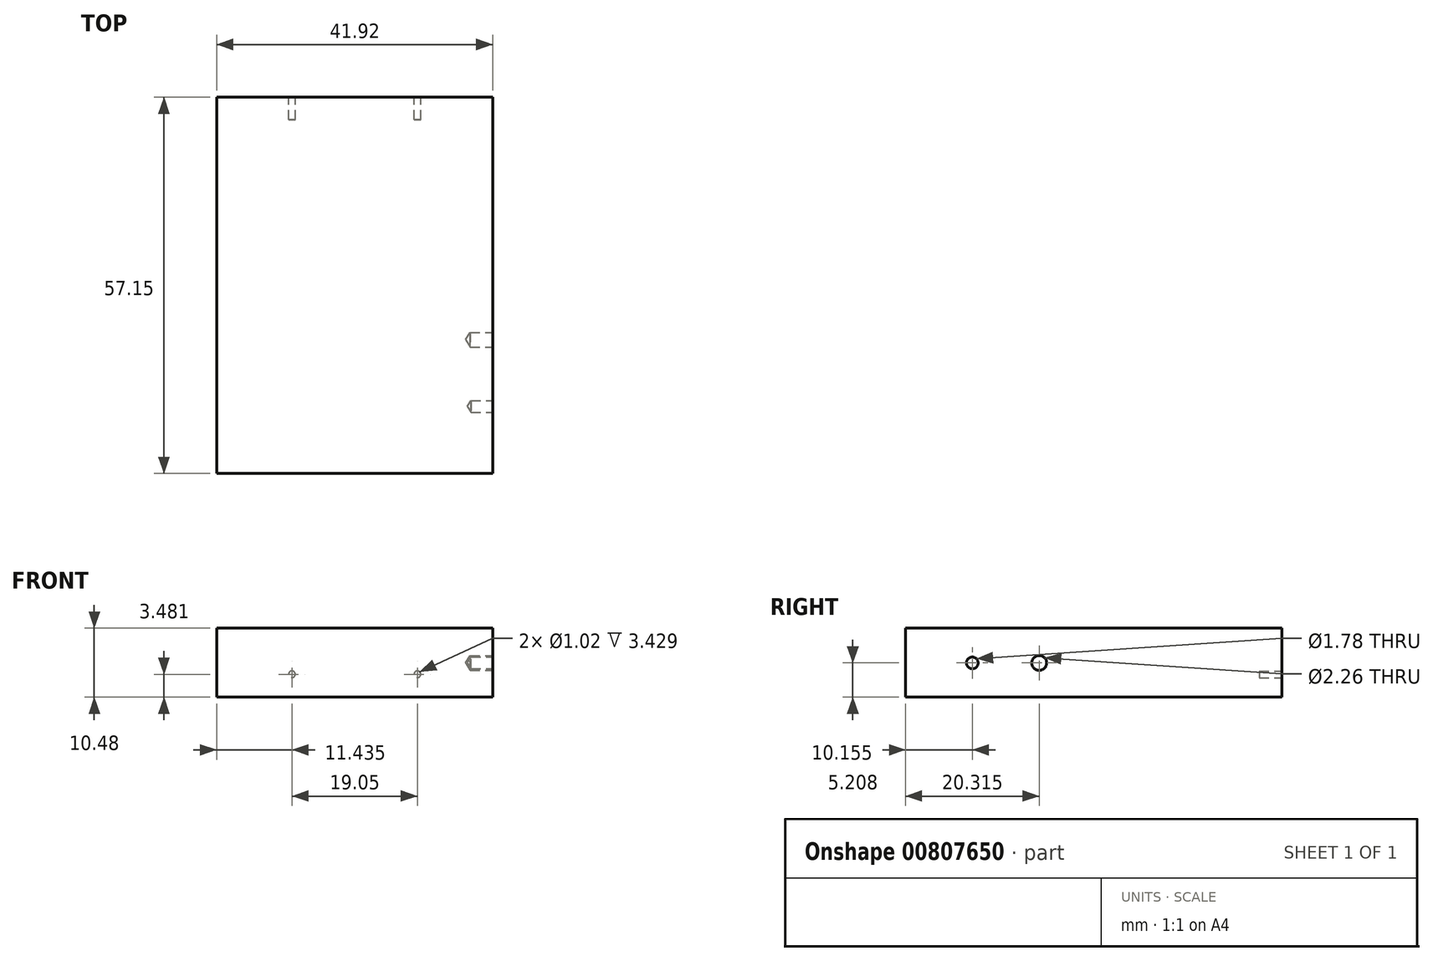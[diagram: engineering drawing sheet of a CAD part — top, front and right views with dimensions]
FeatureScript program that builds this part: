
annotation { "Feature Type Name" : "Feature", "Feature Type Description" : "" }
export const myFeature = defineFeature(function(context is Context, id is Id, definition is map)
    precondition{}
    {
        {
            var Q0;
            Q0=qCreatedBy(makeId("Top.planeOp"),FACE);
            var sketch = newSketch(context, id + "F0", { "sketchPlane" : qUnion([Q0])});
            skLineSegment(sketch, "E0.bottom", {"start": v(-20.96, -28.58) * mm, "end": v(20.95, -28.58) * mm});
            skLineSegment(sketch, "E0.top", {"start": v(-20.95, 28.57) * mm, "end": v(20.96, 28.57) * mm});
            skLineSegment(sketch, "E0.left", {"start": v(-20.96, -28.58) * mm, "end": v(-20.95, 28.57) * mm});
            skLineSegment(sketch, "E0.right", {"start": v(20.95, -28.58) * mm, "end": v(20.96, 28.57) * mm});
            skLineSegment(sketch, "E1", {"start": v(-20.96, -28.58) * mm, "end": v(20.96, 28.58) * mm});
            skSolve(sketch);
        }
        {
            var Q0;
            Q0 = qSketchRegion(id + "F0", true);
            extrude(context, id + "F1", {"entities" : qUnion([Q0]), "endBound" : BoundingType.SYMMETRIC, "depth" : 10.48 * mm, "offsetDistance" : 25.4 * mm});
        }
        {
            var Q0;
            Q0=makeQuery(id+"F1.opExtrude","SWEPT_FACE",FACE,{"disambiguationData":[OSD([sQuery(id+"F0.wireOp",EDGE,"E0.top")])]});
            var sketch = newSketch(context, id + "F2", { "sketchPlane" : qUnion([Q0])});
            skCircle(sketch, "E2", {"center": v(-9.53, -1.76) * mm, "radius": 0.5 * mm});
            skCircle(sketch, "E3", {"center": v(9.52, -1.76) * mm, "radius": 0.5 * mm});
            skSolve(sketch);
        }
        {
            var Q0;
            Q0 = qSketchRegion(id + "F2", true);
            extrude(context, id + "F3", {"entities" : qUnion([Q0]), "operationType" : NewBodyOperationType.REMOVE, "oppositeDirection" : true, "depth" : 3.43 * mm, "offsetDistance" : 25.4 * mm});
        }
        {
            var Q0;
            Q0=makeQuery(id+"F1.opExtrude","SWEPT_FACE",FACE,{"disambiguationData":[OSD([sQuery(id+"F0.wireOp",EDGE,"E0.right")])]});
            var sketch = newSketch(context, id + "F4", { "sketchPlane" : qUnion([Q0])});
            skPoint(sketch, "E4", {"position": v(-18.41, -0.03) * mm});
            skSolve(sketch);
        }
        {
            var Q0;
            Q0=sQuery(id+"F4.wireOp",VERTEX,"E4");
            var Q1;
            Q1=makeQuery(id+"F1.opExtrude","SWEPT_BODY",BODY,{"disambiguationData":[OSD([sQuery(id+"F0.wireOp",EDGE,"E0.bottom"),sQuery(id+"F0.wireOp",EDGE,"E0.top"),sQuery(id+"F0.wireOp",EDGE,"E0.left"),sQuery(id+"F0.wireOp",EDGE,"E0.right")])]});
            hole(context, id + "F5", {"style" : HoleStyle.SIMPLE, "endStyle" : HoleEndStyle.BLIND, "standardTappedOrClearance" : lookupTablePath({ "standard" : "ANSI", "engagement" : "75%", "pitch" : "56 tpi", "size" : "#2", "type" : "Tapped" }), "standardBlindInLast" : lookupTablePath({ "standard" : "ANSI", "engagement" : "75%", "pitch" : "56 tpi", "size" : "#2", "type" : "Tapped" }), "holeDiameter" : 1.78 * mm, "majorDiameter" : 2.18 * mm, "showTappedDepth" : true, "holeDepth" : 3.3 * mm, "isTappedThrough" : true, "tappedDepth" : 1.94 * mm, "tapClearance" : 3, "locations" : qUnion([Q0]), "scope" : qUnion([Q1])});
        }
        {
            var Q0;
            Q0=makeQuery(id+"F1.opExtrude","SWEPT_FACE",FACE,{"disambiguationData":[OSD([sQuery(id+"F0.wireOp",EDGE,"E0.right")])]});
            var sketch = newSketch(context, id + "F6", { "sketchPlane" : qUnion([Q0])});
            skPoint(sketch, "E5", {"position": v(-8.25, -0.03) * mm});
            skSolve(sketch);
        }
        {
            var Q0;
            Q0=sQuery(id+"F6.wireOp",VERTEX,"E5");
            var Q1;
            Q1=makeQuery(id+"F1.opExtrude","SWEPT_BODY",BODY,{"disambiguationData":[OSD([sQuery(id+"F0.wireOp",EDGE,"E0.bottom"),sQuery(id+"F0.wireOp",EDGE,"E0.top"),sQuery(id+"F0.wireOp",EDGE,"E0.left"),sQuery(id+"F0.wireOp",EDGE,"E0.right")])]});
            hole(context, id + "F7", {"style" : HoleStyle.SIMPLE, "endStyle" : HoleEndStyle.BLIND, "standardTappedOrClearance" : lookupTablePath({ "standard" : "ANSI", "engagement" : "75%", "pitch" : "40 tpi", "size" : "#4", "type" : "Tapped" }), "standardBlindInLast" : lookupTablePath({ "standard" : "ANSI", "engagement" : "75%", "pitch" : "40 tpi", "size" : "#4", "type" : "Tapped" }), "holeDiameter" : 2.26 * mm, "majorDiameter" : 2.84 * mm, "showTappedDepth" : true, "holeDepth" : 3.43 * mm, "isTappedThrough" : true, "tappedDepth" : 1.52 * mm, "tapClearance" : 3, "locations" : qUnion([Q0]), "scope" : qUnion([Q1])});
        }
    });
